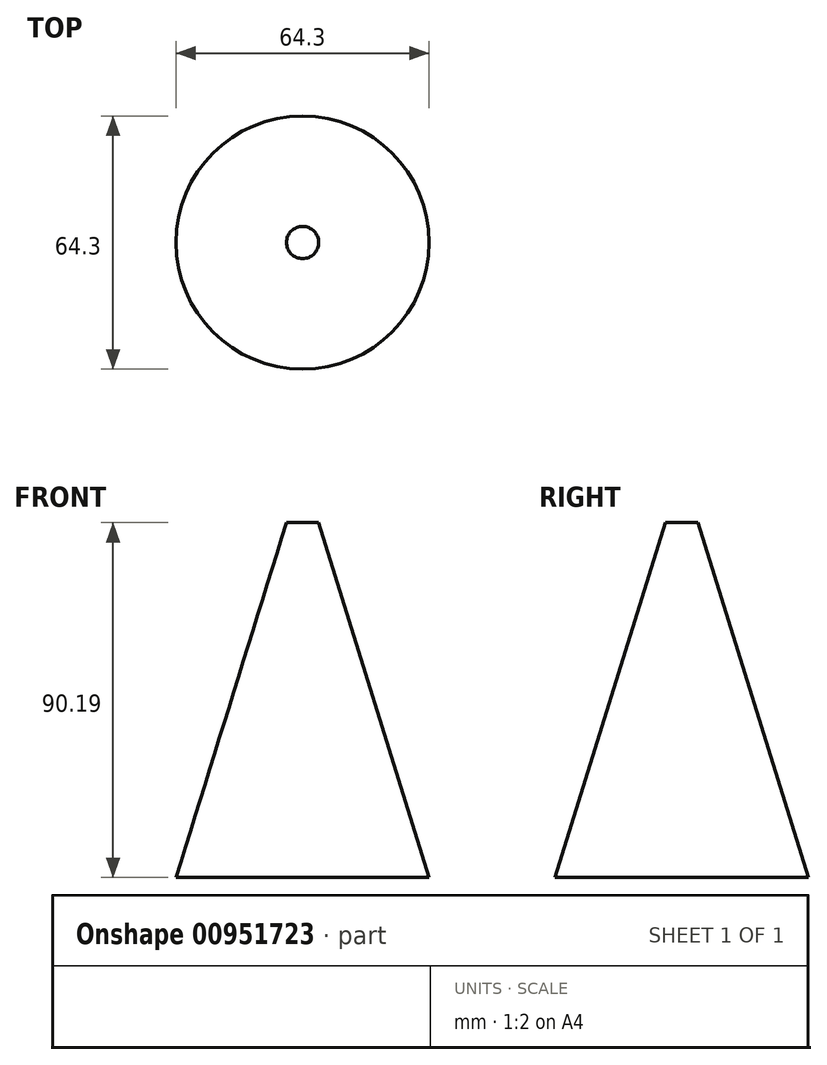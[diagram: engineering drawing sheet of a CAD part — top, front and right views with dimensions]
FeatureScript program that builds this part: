
annotation { "Feature Type Name" : "Feature", "Feature Type Description" : "" }
export const myFeature = defineFeature(function(context is Context, id is Id, definition is map)
    precondition{}
    {
        {
            var Q0;
            Q0=qCreatedBy(makeId("Right.planeOp"),FACE);
            var sketch = newSketch(context, id + "F0", { "sketchPlane" : qUnion([Q0])});
            skLineSegment(sketch, "E0", {"start": v(-4.1, 56.37) * mm, "end": v(-32.15, -33.82) * mm});
            skLineSegment(sketch, "E1", {"start": v(0, 68.4) * mm, "end": v(0, -54.2) * mm, "construction": true});
            skSolve(sketch);
        }
        {
            var Q0;
            Q0=sQuery(id+"F0.wireOp",EDGE,"E0");
            var Q1;
            Q1=sQuery(id+"F0.wireOp",EDGE,"E1");
            revolve(context, id + "F1", {"bodyType" : ToolBodyType.SURFACE, "surfaceOperationType" : NewSurfaceOperationType.NEW, "surfaceEntities" : qUnion([Q0]), "axis" : qUnion([Q1]), "revolveType" : RevolveType.FULL});
        }
    });
